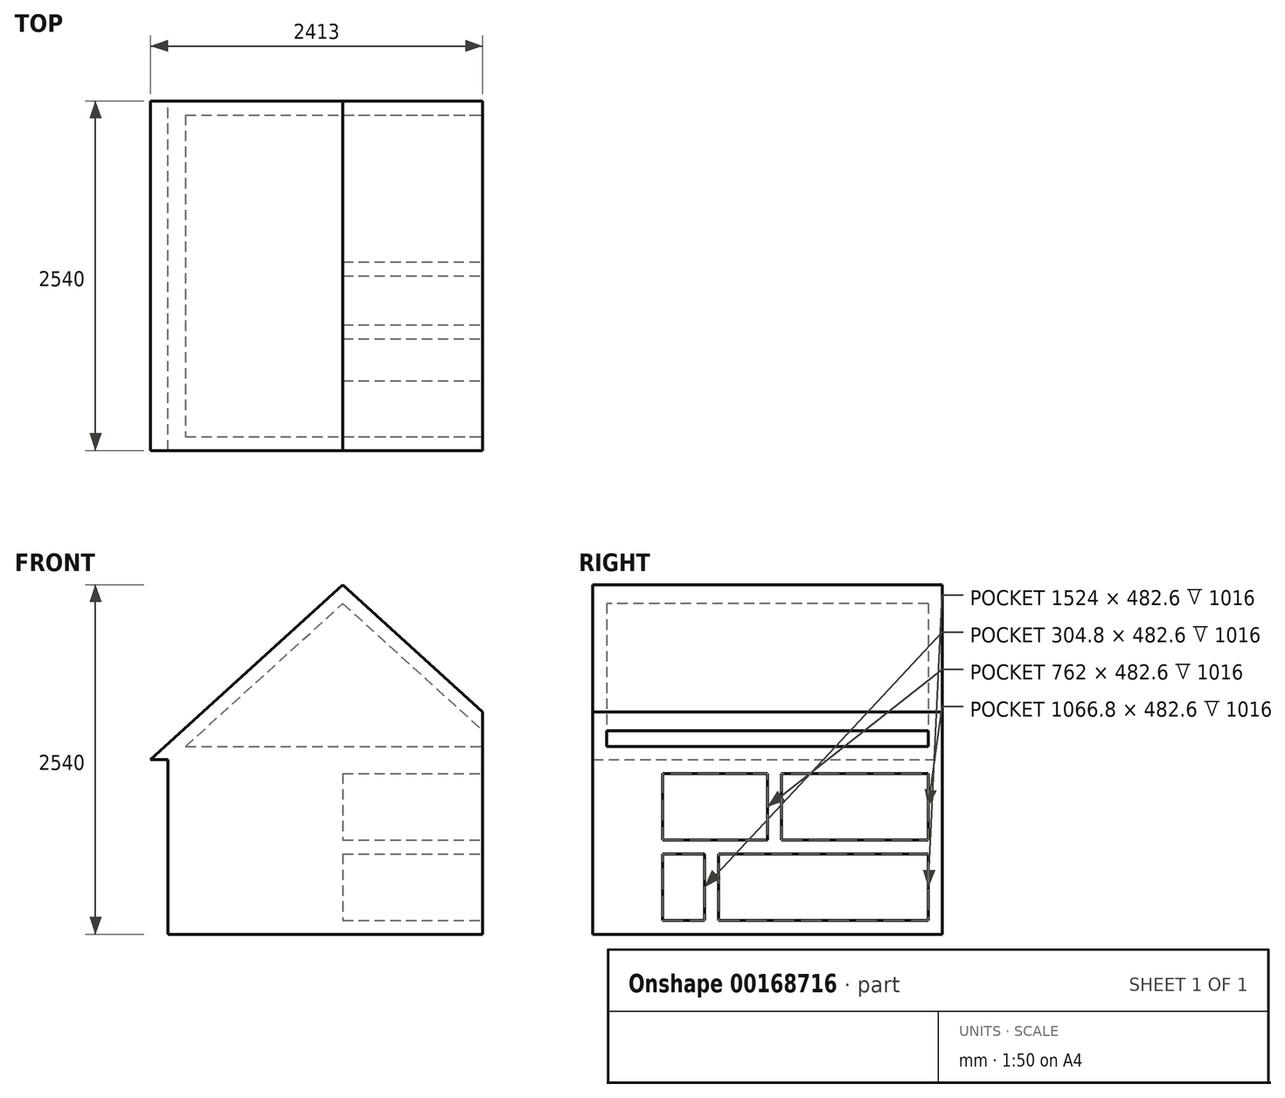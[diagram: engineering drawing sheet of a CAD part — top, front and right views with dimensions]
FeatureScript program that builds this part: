
annotation { "Feature Type Name" : "Feature", "Feature Type Description" : "" }
export const myFeature = defineFeature(function(context is Context, id is Id, definition is map)
    precondition{}
    {
        {
            var Q0;
            Q0=qCreatedBy(makeId("Front.planeOp"),FACE);
            var sketch = newSketch(context, id + "F3", { "sketchPlane" : qUnion([Q0])});
            skLineSegment(sketch, "E0", {"start": v(-1270, -1270) * mm, "end": v(1270, -1270) * mm});
            skLineSegment(sketch, "E1", {"start": v(1270, -1270) * mm, "end": v(1270, 0) * mm});
            skLineSegment(sketch, "E2", {"start": v(1270, 0) * mm, "end": v(1397, 0) * mm});
            skLineSegment(sketch, "E3", {"start": v(1397, 0) * mm, "end": v(0, 1270) * mm});
            skLineSegment(sketch, "E4", {"start": v(0, 1270) * mm, "end": v(-1397, 0) * mm});
            skLineSegment(sketch, "E5", {"start": v(-1397, 0) * mm, "end": v(-1270, 0) * mm});
            skLineSegment(sketch, "E6", {"start": v(-1270, 0) * mm, "end": v(-1270, -1270) * mm});
            skLineSegment(sketch, "E7", {"start": v(0, 1270) * mm, "end": v(0, -1270) * mm, "construction": true});
            skSolve(sketch);
        }
        {
            var Q0;
            Q0 = qSketchRegion(id + "F3", true);
            extrude(context, id + "F4", {"entities" : qUnion([Q0]), "endBound" : BoundingType.SYMMETRIC, "depth" : 2540 * mm});
        }
        {
            var Q0;
            Q0=qCreatedBy(makeId("Front.planeOp"),FACE);
            var sketch = newSketch(context, id + "F5", { "sketchPlane" : qUnion([Q0])});
            skLineSegment(sketch, "E8", {"start": v(-1143, 93.6) * mm, "end": v(0, 1132.7) * mm});
            skLineSegment(sketch, "E9", {"start": v(0, 1132.7) * mm, "end": v(1143, 93.6) * mm});
            skLineSegment(sketch, "E10", {"start": v(-1143, 93.6) * mm, "end": v(1143, 93.6) * mm});
            skSolve(sketch);
        }
        {
            var Q0;
            Q0 = qSketchRegion(id + "F5", true);
            extrude(context, id + "F6", {"entities" : qUnion([Q0]), "operationType" : NewBodyOperationType.REMOVE, "endBound" : BoundingType.SYMMETRIC, "oppositeDirection" : true, "depth" : 2336.8 * mm});
        }
        {
            var Q0;
            Q0=makeQuery(id+"F4.opExtrude","SWEPT_FACE",FACE,{"disambiguationData":[OSD([sQuery(id+"F3.wireOp",EDGE,"E1")])]});
            cPlane(context, id + "F0", {"entities" : qUnion([Q0]), "cplaneType" : CPlaneType.OFFSET, "offset" : 101.6 * mm, "oppositeDirection" : true, "width" : 152.4 * mm, "height" : 152.4 * mm});
        }
        {
            var Q0;
            Q0=qCreatedBy(id+"F0.planeOp",FACE);
            var sketch = newSketch(context, id + "F1", { "sketchPlane" : qUnion([Q0])});
            skLineSegment(sketch, "E11.bottom", {"start": v(1168.4, -101.6) * mm, "end": v(101.6, -101.6) * mm});
            skLineSegment(sketch, "E11.top", {"start": v(1168.4, -584.2) * mm, "end": v(101.6, -584.2) * mm});
            skLineSegment(sketch, "E11.left", {"start": v(1168.4, -101.6) * mm, "end": v(1168.4, -584.2) * mm});
            skLineSegment(sketch, "E11.right", {"start": v(101.6, -101.6) * mm, "end": v(101.6, -584.2) * mm});
            skLineSegment(sketch, "E12.bottom", {"start": v(0, -101.6) * mm, "end": v(-762, -101.6) * mm});
            skLineSegment(sketch, "E12.top", {"start": v(0, -584.2) * mm, "end": v(-762, -584.2) * mm});
            skLineSegment(sketch, "E12.left", {"start": v(0, -101.6) * mm, "end": v(0, -584.2) * mm});
            skLineSegment(sketch, "E12.right", {"start": v(-762, -101.6) * mm, "end": v(-762, -584.2) * mm});
            skLineSegment(sketch, "E13.bottom", {"start": v(-762, -685.8) * mm, "end": v(-457.2, -685.8) * mm});
            skLineSegment(sketch, "E13.top", {"start": v(-762, -1168.4) * mm, "end": v(-457.2, -1168.4) * mm});
            skLineSegment(sketch, "E13.left", {"start": v(-762, -685.8) * mm, "end": v(-762, -1168.4) * mm});
            skLineSegment(sketch, "E13.right", {"start": v(-457.2, -685.8) * mm, "end": v(-457.2, -1168.4) * mm});
            skLineSegment(sketch, "E14.bottom", {"start": v(-355.6, -685.8) * mm, "end": v(1168.4, -685.8) * mm});
            skLineSegment(sketch, "E14.top", {"start": v(-355.6, -1168.4) * mm, "end": v(1168.4, -1168.4) * mm});
            skLineSegment(sketch, "E14.left", {"start": v(-355.6, -685.8) * mm, "end": v(-355.6, -1168.4) * mm});
            skLineSegment(sketch, "E14.right", {"start": v(1168.4, -685.8) * mm, "end": v(1168.4, -1168.4) * mm});
            skLineSegment(sketch, "E15", {"start": v(-762, -685.8) * mm, "end": v(-863.6, -685.8) * mm, "construction": true});
            skLineSegment(sketch, "E16", {"start": v(-863.6, -685.8) * mm, "end": v(-1168.4, -685.8) * mm, "construction": true});
            skLineSegment(sketch, "E17", {"start": v(-1168.4, -685.8) * mm, "end": v(-1270, -685.8) * mm, "construction": true});
            skLineSegment(sketch, "E18", {"start": v(-457.2, -685.8) * mm, "end": v(-355.6, -685.8) * mm, "construction": true});
            skSolve(sketch);
        }
        {
            var Q0;
            Q0 = qSketchRegion(id + "F1", true);
            extrude(context, id + "F7", {"entities" : qUnion([Q0]), "operationType" : NewBodyOperationType.REMOVE, "oppositeDirection" : true, "depth" : 1168.4 * mm});
        }
        {
            var Q0;
            Q0=makeQuery(id+"F4.opExtrude","SWEPT_FACE",FACE,{"disambiguationData":[OSD([sQuery(id+"F3.wireOp",EDGE,"E1")])]});
            var sketch = newSketch(context, id + "F2", { "sketchPlane" : qUnion([Q0])});
            skLineSegment(sketch, "E19.bottom", {"start": v(-1469.52, 1905.64) * mm, "end": v(1690.74, 1905.64) * mm});
            skLineSegment(sketch, "E19.top", {"start": v(-1469.52, -1573.81) * mm, "end": v(1690.74, -1573.81) * mm});
            skLineSegment(sketch, "E19.left", {"start": v(-1469.52, 1905.64) * mm, "end": v(-1469.52, -1573.81) * mm});
            skLineSegment(sketch, "E19.right", {"start": v(1690.74, 1905.64) * mm, "end": v(1690.74, -1573.81) * mm});
            skSolve(sketch);
        }
        {
            var Q0;
            Q0 = qSketchRegion(id + "F2", true);
            extrude(context, id + "F8", {"entities" : qUnion([Q0]), "operationType" : NewBodyOperationType.REMOVE, "endBound" : BoundingType.SYMMETRIC, "oppositeDirection" : true, "depth" : 508 * mm});
        }
    });
